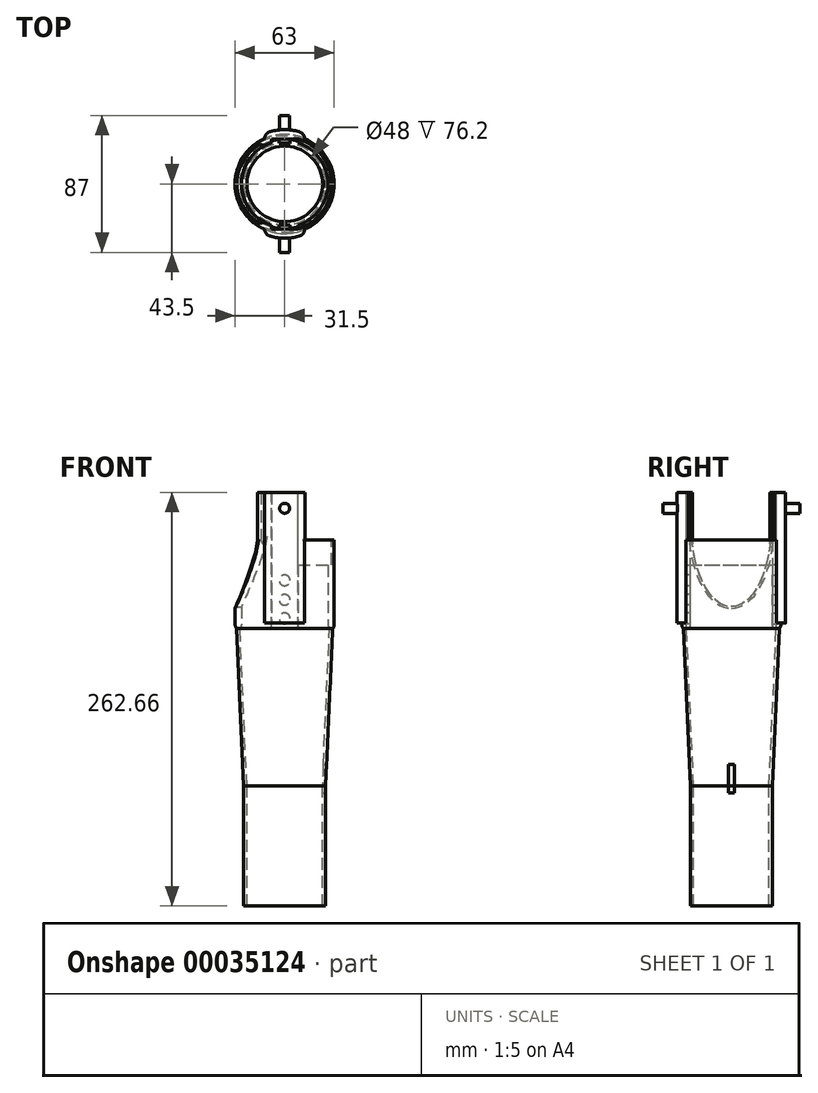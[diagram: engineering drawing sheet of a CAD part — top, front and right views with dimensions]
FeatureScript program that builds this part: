
annotation { "Feature Type Name" : "Feature", "Feature Type Description" : "" }
export const myFeature = defineFeature(function(context is Context, id is Id, definition is map)
    precondition{}
    {
        {
            var Q0;
            Q0=qCreatedBy(makeId("Top.planeOp"),FACE);
            var sketch = newSketch(context, id + "F0", { "sketchPlane" : qUnion([Q0])});
            skCircle(sketch, "E0", {"center": v(0, 0) * mm, "radius": 26 * mm});
            skSolve(sketch);
        }
        {
            var Q0;
            Q0=makeQuery(id+"F0.imprint","IMPRINT",FACE,{"disambiguationData":[TD([[makeQuery(id+"F0.imprint","IMPRINT",EDGE,{"derivedFrom":sQuery(id+"F0.wireOp",EDGE,"E0")}),1.0]])]});
            extrude(context, id + "F1", {"entities" : qUnion([Q0]), "depth" : 76.2 * mm});
        }
        {
            var Q0;
            Q0=makeQuery(id+"F1.opExtrude","CAP_FACE",FACE,{"disambiguationData":[OSD([sQuery(id+"F0.wireOp",EDGE,"E0")])],"isStart":false});
            cPlane(context, id + "F2", {"entities" : qUnion([Q0]), "cplaneType" : CPlaneType.OFFSET, "offset" : 0 * mm, "width" : 150 * mm, "height" : 150 * mm});
        }
        {
            var Q0;
            Q0=qCreatedBy(id+"F2.planeOp",FACE);
            var sketch = newSketch(context, id + "F3", { "sketchPlane" : qUnion([Q0])});
            skCircle(sketch, "E1.0", {"center": v(0, 0) * mm, "radius": 26 * mm});
            skSolve(sketch);
        }
        {
            var Q0;
            Q0=qCreatedBy(id+"F2.planeOp",FACE);
            cPlane(context, id + "F4", {"entities" : qUnion([Q0]), "cplaneType" : CPlaneType.OFFSET, "offset" : 100 * mm, "width" : 150 * mm, "height" : 150 * mm});
        }
        {
            var Q0;
            Q0=qCreatedBy(id+"F4.planeOp",FACE);
            var sketch = newSketch(context, id + "F5", { "sketchPlane" : qUnion([Q0])});
            skCircle(sketch, "E2", {"center": v(0, 0) * mm, "radius": 30.5 * mm});
            skSolve(sketch);
        }
        {
            var Q1;
            Q1=makeQuery(id+"F3.imprint","IMPRINT",FACE,{"disambiguationData":[TD([[makeQuery(id+"F3.imprint","IMPRINT",EDGE,{"derivedFrom":sQuery(id+"F3.wireOp",EDGE,"E1.0")}),1.0]])]});
            var Q2;
            Q2=makeQuery(id+"F5.imprint","IMPRINT",FACE,{"disambiguationData":[TD([[makeQuery(id+"F5.imprint","IMPRINT",EDGE,{"derivedFrom":sQuery(id+"F5.wireOp",EDGE,"E2")}),1.0]])]});
            loft(context, id + "F6", {"operationType" : NewBodyOperationType.ADD, "sheetProfilesArray" : [{ "sheetProfileEntities" : qUnion([Q1]) }, { "sheetProfileEntities" : qUnion([Q2]) }]});
        }
        {
            var Q0;
            Q0=qCreatedBy(id+"F2.planeOp",FACE);
            var sketch = newSketch(context, id + "F7", { "sketchPlane" : qUnion([Q0])});
            skCircle(sketch, "E3", {"center": v(0, 0) * mm, "radius": 24 * mm});
            skSolve(sketch);
        }
        {
            var Q0;
            Q0=qCreatedBy(id+"F4.planeOp",FACE);
            var sketch = newSketch(context, id + "F8", { "sketchPlane" : qUnion([Q0])});
            skCircle(sketch, "E4", {"center": v(0, 0) * mm, "radius": 28.5 * mm});
            skSolve(sketch);
        }
        {
            var Q1;
            Q1=makeQuery(id+"F8.imprint","IMPRINT",FACE,{"disambiguationData":[TD([[makeQuery(id+"F8.imprint","IMPRINT",EDGE,{"derivedFrom":sQuery(id+"F8.wireOp",EDGE,"E4")}),1.0]])]});
            var Q2;
            Q2 = qSketchRegion(id + "F7", true);
            loft(context, id + "F9", {"operationType" : NewBodyOperationType.REMOVE, "sheetProfilesArray" : [{ "sheetProfileEntities" : qUnion([Q1]) }, { "sheetProfileEntities" : qUnion([Q2]) }]});
        }
        {
            var Q0;
            Q0=qCreatedBy(makeId("Top.planeOp"),FACE);
            var sketch = newSketch(context, id + "F10", { "sketchPlane" : qUnion([Q0])});
            skCircle(sketch, "E5", {"center": v(0, 0) * mm, "radius": 24 * mm});
            skSolve(sketch);
        }
        {
            var Q1;
            Q1 = qSketchRegion(id + "F7", true);
            var Q2;
            Q2 = qSketchRegion(id + "F10", true);
            loft(context, id + "F11", {"operationType" : NewBodyOperationType.REMOVE, "sheetProfilesArray" : [{ "sheetProfileEntities" : qUnion([Q1]) }, { "sheetProfileEntities" : qUnion([Q2]) }]});
        }
        {
            var Q0;
            Q0=qCreatedBy(id+"F4.planeOp",FACE);
            var sketch = newSketch(context, id + "F12", { "sketchPlane" : qUnion([Q0])});
            skCircle(sketch, "E6", {"center": v(0, 0) * mm, "radius": 31.5 * mm});
            skCircle(sketch, "E7.0", {"center": v(0, 0) * mm, "radius": 27.5 * mm});
            skSolve(sketch);
        }
        {
            var Q0;
            Q0 = qSketchRegion(id + "F12", true);
            extrude(context, id + "F13", {"entities" : qUnion([Q0]), "operationType" : NewBodyOperationType.ADD, "depth" : 56.46 * mm});
        }
        {
            var Q0;
            Q0=makeQuery(id+"F13.opExtrude","CAP_EDGE",EDGE,{"disambiguationData":[OSD([sQuery(id+"F12.wireOp",EDGE,"E6")])],"isStart":true});
            fillet(context, id + "F14", {"entities" : qUnion([Q0]), "radius" : 5 * mm, "tangentPropagation" : true, "allowEdgeOverflow" : false});
        }
        {
            var Q0;
            Q0=makeQuery(id+"F13.opExtrude","CAP_FACE",FACE,{"disambiguationData":[OSD([sQuery(id+"F12.wireOp",EDGE,"E6"),sQuery(id+"F12.wireOp",EDGE,"E7.0")])],"isStart":false});
            cPlane(context, id + "F15", {"entities" : qUnion([Q0]), "cplaneType" : CPlaneType.OFFSET, "offset" : 0 * mm, "width" : 150 * mm, "height" : 150 * mm});
        }
        {
            var Q0;
            Q0=qCreatedBy(id+"F15.planeOp",FACE);
            var sketch = newSketch(context, id + "F16", { "sketchPlane" : qUnion([Q0])});
            skCircle(sketch, "E8.0", {"center": v(0, 0) * mm, "radius": 31.5 * mm, "construction": true});
            skCircle(sketch, "E9.0", {"center": v(0, 0) * mm, "radius": 27.5 * mm, "construction": true});
            skArc(sketch, "E10", {"start": v(8.5, -28.5) * mm, "mid": v(29.74, 0) * mm, "end": v(8.5, 28.5) * mm});
            skArc(sketch, "E11", {"start": v(8.5, -24.3) * mm, "mid": v(25.75, 0) * mm, "end": v(8.5, 24.3) * mm});
            skLineSegment(sketch, "E12", {"start": v(8.5, 28.5) * mm, "end": v(8.5, 24.3) * mm});
            skLineSegment(sketch, "E13.MirrorCS", {"start": v(8.5, -28.5) * mm, "end": v(8.5, -24.3) * mm});
            skPoint(sketch, "E14.orphan", {"position": v(0, 29.74) * mm});
            skPoint(sketch, "E15.orphan", {"position": v(0, -25.75) * mm});
            skSolve(sketch);
        }
        {
            var Q0;
            Q0 = qSketchRegion(id + "F16", true);
            extrude(context, id + "F17", {"entities" : qUnion([Q0]), "operationType" : NewBodyOperationType.REMOVE, "oppositeDirection" : true, "depth" : 16 * mm});
        }
        {
            var Q0;
            Q0=qCreatedBy(id+"F15.planeOp",FACE);
            var sketch = newSketch(context, id + "F18", { "sketchPlane" : qUnion([Q0])});
            skLineSegment(sketch, "E16.bottom", {"start": v(-8.5, 28.5) * mm, "end": v(8.5, 28.5) * mm});
            skLineSegment(sketch, "E16.top", {"start": v(-8.5, 24) * mm, "end": v(8.5, 24) * mm});
            skLineSegment(sketch, "E16.left", {"start": v(-8.5, 28.5) * mm, "end": v(-8.5, 24) * mm});
            skLineSegment(sketch, "E16.right", {"start": v(8.5, 28.5) * mm, "end": v(8.5, 24) * mm});
            skLineSegment(sketch, "E17", {"start": v(0, 28.5) * mm, "end": v(0, 24) * mm, "construction": true});
            skLineSegment(sketch, "E18.0", {"start": v(8.5, -28.5) * mm, "end": v(8.5, -28.5) * mm});
            skLineSegment(sketch, "E19.MirrorCS", {"start": v(-8.5, -24) * mm, "end": v(8.5, -24) * mm});
            skLineSegment(sketch, "E20.MirrorCS", {"start": v(8.5, -28.5) * mm, "end": v(8.5, -24) * mm});
            skLineSegment(sketch, "E21.MirrorCS", {"start": v(-8.5, -28.5) * mm, "end": v(8.5, -28.5) * mm});
            skLineSegment(sketch, "E22.MirrorCS", {"start": v(-8.5, -28.5) * mm, "end": v(-8.5, -24) * mm});
            skSolve(sketch);
        }
        {
            var Q0;
            Q0 = qSketchRegion(id + "F18", true);
            extrude(context, id + "F19", {"entities" : qUnion([Q0]), "operationType" : NewBodyOperationType.REMOVE, "oppositeDirection" : true, "depth" : 56.46 * mm});
        }
        {
            var Q0;
            {var subQ0=sQuery(id+"F12.wireOp",EDGE,"E7.0");Q0=makeQuery(id+"F19.boolean.opBoolean","SPLIT",EDGE,{"disambiguationData":[TD([makeQuery(id+"F19.opExtrude","SWEPT_FACE",FACE,{"disambiguationData":[OSD([sQuery(id+"F18.wireOp",EDGE,"E16.left")])]})])],"derivedFrom":makeQuery(id+"F13.opExtrude","CAP_EDGE",EDGE,{"disambiguationData":[OSD([subQ0])],"isStart":true})});}
            var Q1;
            {var subQ0=sQuery(id+"F12.wireOp",EDGE,"E7.0");Q1=makeQuery(id+"F19.boolean.opBoolean","SPLIT",EDGE,{"disambiguationData":[TD([makeQuery(id+"F19.opExtrude","SWEPT_FACE",FACE,{"disambiguationData":[OSD([sQuery(id+"F18.wireOp",EDGE,"E16.right")])]})])],"derivedFrom":makeQuery(id+"F13.opExtrude","CAP_EDGE",EDGE,{"disambiguationData":[OSD([subQ0])],"isStart":true})});}
            fillet(context, id + "F20", {"entities" : qUnion([Q0, Q1]), "radius" : 5 * mm, "tangentPropagation" : true, "allowEdgeOverflow" : false});
        }
        {
            var Q0;
            Q0=makeQuery(id+"F19.boolean.opBoolean","COPY",FACE,{"derivedFrom":makeQuery(id+"F19.opExtrude","SWEPT_FACE",FACE,{"disambiguationData":[OSD([sQuery(id+"F18.wireOp",EDGE,"E16.bottom")])]})});
            cPlane(context, id + "F21", {"entities" : qUnion([Q0]), "cplaneType" : CPlaneType.OFFSET, "offset" : 0 * mm, "width" : 150 * mm, "height" : 150 * mm});
        }
        {
            var Q0;
            Q0=qCreatedBy(id+"F21.planeOp",FACE);
            var sketch = newSketch(context, id + "F22", { "sketchPlane" : qUnion([Q0])});
            skLineSegment(sketch, "E23.0.0", {"start": v(8.5, 232.66) * mm, "end": v(-8.5, 232.66) * mm, "construction": true});
            skLineSegment(sketch, "E23.0.1", {"start": v(-8.5, 232.66) * mm, "end": v(-8.5, 176.2) * mm, "construction": true});
            skLineSegment(sketch, "E23.0.2", {"start": v(-8.5, 176.2) * mm, "end": v(0, 176.2) * mm, "construction": true});
            skLineSegment(sketch, "E23.0.3", {"start": v(0, 176.2) * mm, "end": v(8.5, 176.2) * mm, "construction": true});
            skLineSegment(sketch, "E23.0.4", {"start": v(8.5, 176.2) * mm, "end": v(8.5, 232.66) * mm, "construction": true});
            skLineSegment(sketch, "E24", {"start": v(0, 232.66) * mm, "end": v(0, 176.2) * mm, "construction": true});
            skCircle(sketch, "E25", {"center": v(0, 206.85) * mm, "radius": 3.45 * mm});
            skCircle(sketch, "E26", {"center": v(0, 194.54) * mm, "radius": 3.45 * mm});
            skCircle(sketch, "E27", {"center": v(0, 182.7) * mm, "radius": 3.45 * mm});
            skSolve(sketch);
        }
        {
            var Q0;
            Q0 = qSketchRegion(id + "F22", true);
            extrude(context, id + "F23", {"entities" : qUnion([Q0]), "depth" : 2.5 * mm});
        }
        {
            var Q0;
            Q0=makeQuery(id+"F23.opExtrude","SWEPT_BODY",BODY,{"disambiguationData":[OSD([sQuery(id+"F22.wireOp",EDGE,"E25")])]});
            var Q1;
            Q1=makeQuery(id+"F23.opExtrude","SWEPT_BODY",BODY,{"disambiguationData":[OSD([sQuery(id+"F22.wireOp",EDGE,"E26")])]});
            var Q2;
            Q2=makeQuery(id+"F23.opExtrude","SWEPT_BODY",BODY,{"disambiguationData":[OSD([sQuery(id+"F22.wireOp",EDGE,"E27")])]});
            var Q3;
            Q3=qCreatedBy(makeId("Front.planeOp"),FACE);
            mirror(context, id + "F24", {"operationType" : NewBodyOperationType.ADD, "entities" : qUnion([Q0, Q1, Q2]), "mirrorPlane" : qUnion([Q3])});
        }
        {
            var Q0;
            Q0=qCreatedBy(id+"F15.planeOp",FACE);
            var sketch = newSketch(context, id + "F25", { "sketchPlane" : qUnion([Q0])});
            skCircle(sketch, "E28", {"center": v(0, 0) * mm, "radius": 34.44 * mm});
            skCircle(sketch, "E29.0", {"center": v(0, 0) * mm, "radius": 31.5 * mm});
            skLineSegment(sketch, "E30", {"start": v(12.77, 31.98) * mm, "end": v(12.77, 28.8) * mm});
            skLineSegment(sketch, "E31.MirrorCS", {"start": v(-12.77, 31.98) * mm, "end": v(-12.77, 28.8) * mm});
            skLineSegment(sketch, "E32.MirrorCS", {"start": v(12.77, -31.98) * mm, "end": v(12.77, -28.8) * mm});
            skLineSegment(sketch, "E33.MirrorCS", {"start": v(-12.77, -31.98) * mm, "end": v(-12.77, -28.8) * mm});
            skSolve(sketch);
        }
        {
            var Q0;
            {var subQ1=sQuery(id+"F25.wireOp",EDGE,"E30");Q0=makeQuery(id+"F25.imprint","IMPRINT",FACE,{"disambiguationData":[TD([[makeQuery(id+"F25.imprint","IMPRINT",EDGE,{"derivedFrom":subQ1}),-1.0]])]});}
            var Q1;
            {var subQ1=sQuery(id+"F25.wireOp",EDGE,"E32.MirrorCS");Q1=makeQuery(id+"F25.imprint","IMPRINT",FACE,{"disambiguationData":[TD([[makeQuery(id+"F25.imprint","IMPRINT",EDGE,{"derivedFrom":subQ1}),1.0]])]});}
            extrude(context, id + "F26", {"entities" : qUnion([Q0, Q1]), "operationType" : NewBodyOperationType.ADD, "depth" : 30 * mm, "hasSecondDirection" : true, "secondDirectionOppositeDirection" : true, "secondDirectionDepth" : 53 * mm});
        }
        {
            var Q0;
            Q0=makeQuery(id+"F13.opExtrude","CAP_FACE",FACE,{"disambiguationData":[OSD([sQuery(id+"F12.wireOp",EDGE,"E6"),sQuery(id+"F12.wireOp",EDGE,"E7.0")])],"isStart":false});
            var sketch = newSketch(context, id + "F27", { "sketchPlane" : qUnion([Q0])});
            skLineSegment(sketch, "E34", {"start": v(12.77, 28.8) * mm, "end": v(12.77, 26.86) * mm});
            skLineSegment(sketch, "E35", {"start": v(-12.77, 28.8) * mm, "end": v(-12.77, 24.35) * mm});
            skLineSegment(sketch, "E36.MirrorCS", {"start": v(12.77, -28.8) * mm, "end": v(12.77, -26.86) * mm});
            skLineSegment(sketch, "E37.MirrorCS", {"start": v(-12.77, -28.8) * mm, "end": v(-12.77, -24.35) * mm});
            skSolve(sketch);
        }
        {
            var Q0;
            {var subQ5=sQuery(id+"F27.wireOp",EDGE,"E34");Q0=makeQuery(id+"F27.imprint","IMPRINT",FACE,{"disambiguationData":[TD([[makeQuery(id+"F27.imprint","IMPRINT",EDGE,{"derivedFrom":subQ5}),-1.0]])]});}
            var Q1;
            {var subQ9=sQuery(id+"F27.wireOp",EDGE,"E36.MirrorCS");Q1=makeQuery(id+"F27.imprint","IMPRINT",FACE,{"disambiguationData":[TD([[makeQuery(id+"F27.imprint","IMPRINT",EDGE,{"derivedFrom":subQ9}),1.0]])]});}
            extrude(context, id + "F28", {"entities" : qUnion([Q0, Q1]), "operationType" : NewBodyOperationType.ADD, "depth" : 30 * mm, "hasSecondDirection" : true, "secondDirectionOppositeDirection" : true, "secondDirectionDepth" : 25 * mm});
        }
        {
            var Q0;
            Q0=makeQuery(id+"F26.opExtrude","SWEPT_EDGE",EDGE,{"disambiguationData":[OSD([sQuery(id+"F25.wireOp",EDGE,"E28"),sQuery(id+"F25.wireOp",EDGE,"E31.MirrorCS")])]});
            var Q1;
            Q1=makeQuery(id+"F26.opExtrude","SWEPT_EDGE",EDGE,{"disambiguationData":[OSD([sQuery(id+"F25.wireOp",EDGE,"E28"),sQuery(id+"F25.wireOp",EDGE,"E33.MirrorCS")])]});
            var Q2;
            Q2=makeQuery(id+"F26.opExtrude","SWEPT_EDGE",EDGE,{"disambiguationData":[OSD([sQuery(id+"F25.wireOp",EDGE,"E28"),sQuery(id+"F25.wireOp",EDGE,"E32.MirrorCS")])]});
            var Q3;
            Q3=makeQuery(id+"F26.opExtrude","SWEPT_EDGE",EDGE,{"disambiguationData":[OSD([sQuery(id+"F25.wireOp",EDGE,"E28"),sQuery(id+"F25.wireOp",EDGE,"E30")])]});
            fillet(context, id + "F29", {"entities" : qUnion([Q0, Q1, Q2, Q3]), "radius" : 5 * mm, "tangentPropagation" : true, "allowEdgeOverflow" : false});
        }
        {
            var Q0;
            Q0=makeQuery(id+"F28.opExtrude","SWEPT_EDGE",EDGE,{"disambiguationData":[OSD([sQuery(id+"F12.wireOp",EDGE,"E7.0"),sQuery(id+"F27.wireOp",EDGE,"E37.MirrorCS")])]});
            fillet(context, id + "F30", {"entities" : qUnion([Q0]), "radius" : 1 * mm, "tangentPropagation" : true, "allowEdgeOverflow" : false});
        }
        {
            var Q0;
            Q0=makeQuery(id+"F28.opExtrude","SWEPT_EDGE",EDGE,{"disambiguationData":[OSD([sQuery(id+"F12.wireOp",EDGE,"E7.0"),sQuery(id+"F27.wireOp",EDGE,"E35")])]});
            fillet(context, id + "F31", {"entities" : qUnion([Q0]), "radius" : 1 * mm, "tangentPropagation" : true, "allowEdgeOverflow" : false});
        }
        {
            var Q0;
            Q0=makeQuery(id+"F28.opExtrude","SWEPT_EDGE",EDGE,{"disambiguationData":[OSD([sQuery(id+"F16.wireOp",EDGE,"E10"),sQuery(id+"F27.wireOp",EDGE,"E36.MirrorCS")])]});
            fillet(context, id + "F32", {"entities" : qUnion([Q0]), "radius" : 1 * mm, "tangentPropagation" : true, "allowEdgeOverflow" : false});
        }
        {
            var Q0;
            Q0=makeQuery(id+"F28.opExtrude","SWEPT_EDGE",EDGE,{"disambiguationData":[OSD([sQuery(id+"F16.wireOp",EDGE,"E10"),sQuery(id+"F27.wireOp",EDGE,"E34")])]});
            fillet(context, id + "F33", {"entities" : qUnion([Q0]), "radius" : 1 * mm, "tangentPropagation" : true, "allowEdgeOverflow" : false});
        }
        {
            var Q0;
            {var subQ0=sQuery(id+"F18.wireOp",EDGE,"E16.bottom");Q0=makeQuery(id+"F28.boolean.opBoolean","MERGE",FACE,{"derivedFrom":[makeQuery(id+"F19.boolean.opBoolean","COPY",FACE,{"derivedFrom":makeQuery(id+"F19.opExtrude","SWEPT_FACE",FACE,{"disambiguationData":[OSD([subQ0])]})}),makeQuery(id+"F28.opExtrude","SWEPT_FACE",FACE,{"disambiguationData":[OSD([subQ0])]})]});}
            var sketch = newSketch(context, id + "F34", { "sketchPlane" : qUnion([Q0])});
            skLineSegment(sketch, "E38.0", {"start": v(-8.5, 262.66) * mm, "end": v(8.5, 262.66) * mm, "construction": true});
            skLineSegment(sketch, "E39", {"start": v(0, 262.66) * mm, "end": v(0, 242.66) * mm, "construction": true});
            skPoint(sketch, "E39.endSnap0", {"position": v(0, 262.66) * mm});
            skCircle(sketch, "E40", {"center": v(0, 252.66) * mm, "radius": 3.18 * mm});
            skSolve(sketch);
        }
        {
            var Q0;
            Q0=makeQuery(id+"F34.imprint","IMPRINT",FACE,{"disambiguationData":[TD([[makeQuery(id+"F34.imprint","IMPRINT",EDGE,{"derivedFrom":sQuery(id+"F34.wireOp",EDGE,"E40")}),1.0]])]});
            extrude(context, id + "F35", {"entities" : qUnion([Q0]), "oppositeDirection" : true, "depth" : 15 * mm});
        }
        {
            var Q0;
            Q0=makeQuery(id+"F35.opExtrude","SWEPT_BODY",BODY,{"disambiguationData":[OSD([sQuery(id+"F34.wireOp",EDGE,"E40")])]});
            var Q1;
            Q1=qCreatedBy(makeId("Front.planeOp"),FACE);
            mirror(context, id + "F36", {"operationType" : NewBodyOperationType.ADD, "entities" : qUnion([Q0]), "mirrorPlane" : qUnion([Q1])});
        }
        {
            var Q0;
            Q0=qCreatedBy(makeId("Right.planeOp"),FACE);
            cPlane(context, id + "F37", {"entities" : qUnion([Q0]), "cplaneType" : CPlaneType.OFFSET, "offset" : 55 * mm, "oppositeDirection" : true, "width" : 150 * mm, "height" : 150 * mm});
        }
        {
            var Q0;
            Q0=qCreatedBy(id+"F37.planeOp",FACE);
            var sketch = newSketch(context, id + "F38", { "sketchPlane" : qUnion([Q0])});
            skLineSegment(sketch, "E41", {"start": v(-31.5, 188.04) * mm, "end": v(-31.5, 188.5) * mm, "construction": true});
            skLineSegment(sketch, "E42", {"start": v(31.5, 188.5) * mm, "end": v(31.5, 188.04) * mm, "construction": true});
            skEllipse(sketch, "E43", {"center": v(0, 241.57) * mm, "majorRadius": 25.3 * mm, "minorRadius": 51.5 * mm, "majorAxis": v(-1, 0)});
            skSolve(sketch);
        }
        {
            var Q0;
            Q0 = qSketchRegion(id + "F38", true);
            extrude(context, id + "F39", {"entities" : qUnion([Q0]), "operationType" : NewBodyOperationType.REMOVE, "depth" : 40 * mm});
        }
        {
            var Q0;
            Q0=makeQuery(id+"F39.boolean.opBoolean","INTERSECT",EDGE,{"derivedFrom":[makeQuery(id+"F13.opExtrude","SWEPT_FACE",FACE,{"disambiguationData":[OSD([sQuery(id+"F12.wireOp",EDGE,"E6")])]}),makeQuery(id+"F39.opExtrude","SWEPT_FACE",FACE,{"disambiguationData":[OSD([sQuery(id+"F38.wireOp",EDGE,"E43")])]})]});
            fillet(context, id + "F40", {"entities" : qUnion([Q0]), "radius" : 1 * mm, "tangentPropagation" : true, "allowEdgeOverflow" : false});
        }
        {
            var Q0;
            {var subQ0=sQuery(id+"F12.wireOp",EDGE,"E6");var subQ1=sQuery(id+"F12.wireOp",EDGE,"E7.0");var subQ6=sQuery(id+"F25.wireOp",EDGE,"E33.MirrorCS");var subQ7=makeQuery(id+"F26.opExtrude","SWEPT_FACE",FACE,{"disambiguationData":[OSD([subQ6])]});Q0=makeQuery(id+"F39.boolean.opBoolean","SPLIT",FACE,{"disambiguationData":[TD([subQ7])],"derivedFrom":makeQuery(id+"F28.boolean.opBoolean","SPLIT",FACE,{"disambiguationData":[TD([makeQuery(id+"F13.opExtrude","SWEPT_FACE",FACE,{"disambiguationData":[OSD([subQ1])]})])],"derivedFrom":makeQuery(id+"F13.opExtrude","CAP_FACE",FACE,{"disambiguationData":[OSD([subQ0,subQ1])],"isStart":false})})});}
            var Q1;
            {var subQ0=sQuery(id+"F12.wireOp",EDGE,"E6");var subQ1=sQuery(id+"F12.wireOp",EDGE,"E7.0");var subQ6=sQuery(id+"F25.wireOp",EDGE,"E31.MirrorCS");var subQ7=makeQuery(id+"F26.opExtrude","SWEPT_FACE",FACE,{"disambiguationData":[OSD([subQ6])]});Q1=makeQuery(id+"F39.boolean.opBoolean","SPLIT",FACE,{"disambiguationData":[TD([subQ7])],"derivedFrom":makeQuery(id+"F28.boolean.opBoolean","SPLIT",FACE,{"disambiguationData":[TD([makeQuery(id+"F13.opExtrude","SWEPT_FACE",FACE,{"disambiguationData":[OSD([subQ1])]})])],"derivedFrom":makeQuery(id+"F13.opExtrude","CAP_FACE",FACE,{"disambiguationData":[OSD([subQ0,subQ1])],"isStart":false})})});}
            var Q2;
            Q2=makeQuery(id+"F28.boolean.opBoolean","MERGE",FACE,{"derivedFrom":[makeQuery(id+"F26.opExtrude","CAP_FACE",FACE,{"disambiguationData":[OSD([sQuery(id+"F25.wireOp",EDGE,"E28"),sQuery(id+"F25.wireOp",EDGE,"E29.0"),sQuery(id+"F25.wireOp",EDGE,"E32.MirrorCS"),sQuery(id+"F25.wireOp",EDGE,"E33.MirrorCS")])],"isStart":false}),makeQuery(id+"F28.opExtrude","CAP_FACE",FACE,{"disambiguationData":[OSD([sQuery(id+"F12.wireOp",EDGE,"E6"),sQuery(id+"F12.wireOp",EDGE,"E7.0"),sQuery(id+"F16.wireOp",EDGE,"E10"),sQuery(id+"F18.wireOp",EDGE,"E20.MirrorCS"),sQuery(id+"F18.wireOp",EDGE,"E21.MirrorCS"),sQuery(id+"F18.wireOp",EDGE,"E22.MirrorCS"),sQuery(id+"F27.wireOp",EDGE,"E36.MirrorCS"),sQuery(id+"F27.wireOp",EDGE,"E37.MirrorCS")])],"isStart":false})]});
            extrude(context, id + "F41", {"entities" : qUnion([Q0, Q1]), "operationType" : NewBodyOperationType.ADD, "endBound" : BoundingType.UP_TO_SURFACE, "endBoundEntityFace" : qUnion([Q2]), "depth" : 25 * mm});
        }
        {
            var Q0;
            {var subQ0=sQuery(id+"F38.wireOp",EDGE,"E43");var subQ1=makeQuery(id+"F39.opExtrude","CAP_FACE",FACE,{"disambiguationData":[OSD([subQ0])],"isStart":false});var subQ2=sQuery(id+"F12.wireOp",EDGE,"E7.0");var subQ3=makeQuery(id+"F13.opExtrude","SWEPT_FACE",FACE,{"disambiguationData":[OSD([subQ2])]});var subQ5=sQuery(id+"F12.wireOp",EDGE,"E6");var subQ7=makeQuery(id+"F13.opExtrude","CAP_EDGE",EDGE,{"disambiguationData":[OSD([subQ2])],"isStart":false});var subQ8=sQuery(id+"F18.wireOp",EDGE,"E16.left");var subQ9=makeQuery(id+"F28.opExtrude","SWEPT_FACE",FACE,{"disambiguationData":[OSD([subQ2]),TDD([makeQuery(id+"F27.imprint","IMPRINT",EDGE,{"disambiguationData":[TD([[makeQuery(id+"F27.imprint","INTERSECT",VERTEX,{"derivedFrom":[makeQuery(id+"F19.boolean.opBoolean","COPY",EDGE,{"derivedFrom":makeQuery(id+"F19.opExtrude","CAP_EDGE",EDGE,{"disambiguationData":[OSD([subQ8])],"isStart":true})}),subQ7]}),1.0]])],"derivedFrom":subQ7})])]});var subQ10=sQuery(id+"F18.wireOp",EDGE,"E22.MirrorCS");var subQ11=makeQuery(id+"F28.opExtrude","SWEPT_FACE",FACE,{"disambiguationData":[OSD([subQ2]),TDD([makeQuery(id+"F27.imprint","IMPRINT",EDGE,{"disambiguationData":[TD([[makeQuery(id+"F27.imprint","INTERSECT",VERTEX,{"derivedFrom":[makeQuery(id+"F19.boolean.opBoolean","COPY",EDGE,{"derivedFrom":makeQuery(id+"F19.opExtrude","CAP_EDGE",EDGE,{"disambiguationData":[OSD([subQ10])],"isStart":true})}),subQ7]}),-1.0]])],"derivedFrom":subQ7})])]});var subQ12=makeQuery(id+"F13.opExtrude","CAP_FACE",FACE,{"disambiguationData":[OSD([subQ5,subQ2])],"isStart":false});var subQ13=makeQuery(id+"F28.boolean.opBoolean","MERGE",FACE,{"derivedFrom":[makeQuery(id+"F19.boolean.opBoolean","SPLIT",FACE,{"disambiguationData":[TD([makeQuery(id+"F19.opExtrude","SWEPT_FACE",FACE,{"disambiguationData":[OSD([subQ8])]})])],"derivedFrom":subQ3}),subQ9,subQ11]});Q0=makeQuery(id+"F41.boolean.opBoolean","MERGE",EDGE,{"derivedFrom":[makeQuery(id+"F39.boolean.opBoolean","INTERSECT",EDGE,{"disambiguationData":[OD(0.0)],"derivedFrom":[subQ13,subQ1]}),makeQuery(id+"F41.opExtrude","SWEPT_EDGE",EDGE,{"disambiguationData":[OSD([subQ5,subQ2,subQ0]),TDD([makeQuery(id+"F39.boolean.opBoolean","INTERSECT",VERTEX,{"disambiguationData":[OD(0.0)],"derivedFrom":[subQ13,makeQuery(id+"F28.boolean.opBoolean","SPLIT",FACE,{"disambiguationData":[TD([subQ3])],"derivedFrom":subQ12}),subQ1]})])]})]});}
            var Q1;
            {var subQ0=sQuery(id+"F38.wireOp",EDGE,"E43");var subQ1=makeQuery(id+"F39.opExtrude","CAP_FACE",FACE,{"disambiguationData":[OSD([subQ0])],"isStart":false});var subQ2=sQuery(id+"F12.wireOp",EDGE,"E7.0");var subQ3=makeQuery(id+"F13.opExtrude","SWEPT_FACE",FACE,{"disambiguationData":[OSD([subQ2])]});var subQ5=sQuery(id+"F12.wireOp",EDGE,"E6");var subQ7=makeQuery(id+"F13.opExtrude","CAP_EDGE",EDGE,{"disambiguationData":[OSD([subQ2])],"isStart":false});var subQ8=sQuery(id+"F18.wireOp",EDGE,"E16.left");var subQ9=makeQuery(id+"F28.opExtrude","SWEPT_FACE",FACE,{"disambiguationData":[OSD([subQ2]),TDD([makeQuery(id+"F27.imprint","IMPRINT",EDGE,{"disambiguationData":[TD([[makeQuery(id+"F27.imprint","INTERSECT",VERTEX,{"derivedFrom":[makeQuery(id+"F19.boolean.opBoolean","COPY",EDGE,{"derivedFrom":makeQuery(id+"F19.opExtrude","CAP_EDGE",EDGE,{"disambiguationData":[OSD([subQ8])],"isStart":true})}),subQ7]}),1.0]])],"derivedFrom":subQ7})])]});var subQ10=sQuery(id+"F18.wireOp",EDGE,"E22.MirrorCS");var subQ11=makeQuery(id+"F28.opExtrude","SWEPT_FACE",FACE,{"disambiguationData":[OSD([subQ2]),TDD([makeQuery(id+"F27.imprint","IMPRINT",EDGE,{"disambiguationData":[TD([[makeQuery(id+"F27.imprint","INTERSECT",VERTEX,{"derivedFrom":[makeQuery(id+"F19.boolean.opBoolean","COPY",EDGE,{"derivedFrom":makeQuery(id+"F19.opExtrude","CAP_EDGE",EDGE,{"disambiguationData":[OSD([subQ10])],"isStart":true})}),subQ7]}),-1.0]])],"derivedFrom":subQ7})])]});var subQ12=makeQuery(id+"F13.opExtrude","CAP_FACE",FACE,{"disambiguationData":[OSD([subQ5,subQ2])],"isStart":false});var subQ13=makeQuery(id+"F28.boolean.opBoolean","MERGE",FACE,{"derivedFrom":[makeQuery(id+"F19.boolean.opBoolean","SPLIT",FACE,{"disambiguationData":[TD([makeQuery(id+"F19.opExtrude","SWEPT_FACE",FACE,{"disambiguationData":[OSD([subQ8])]})])],"derivedFrom":subQ3}),subQ9,subQ11]});Q1=makeQuery(id+"F41.boolean.opBoolean","MERGE",EDGE,{"derivedFrom":[makeQuery(id+"F39.boolean.opBoolean","INTERSECT",EDGE,{"disambiguationData":[OD(1.0)],"derivedFrom":[subQ13,subQ1]}),makeQuery(id+"F41.opExtrude","SWEPT_EDGE",EDGE,{"disambiguationData":[OSD([subQ5,subQ2,subQ0]),TDD([makeQuery(id+"F39.boolean.opBoolean","INTERSECT",VERTEX,{"disambiguationData":[OD(1.0)],"derivedFrom":[subQ13,makeQuery(id+"F28.boolean.opBoolean","SPLIT",FACE,{"disambiguationData":[TD([subQ3])],"derivedFrom":subQ12}),subQ1]})])]})]});}
            fillet(context, id + "F42", {"entities" : qUnion([Q0, Q1]), "radius" : 5 * mm, "tangentPropagation" : true, "allowEdgeOverflow" : false});
        }
        {
            var Q0;
            Q0=qCreatedBy(makeId("Right.planeOp"),FACE);
            cPlane(context, id + "F43", {"entities" : qUnion([Q0]), "cplaneType" : CPlaneType.OFFSET, "offset" : 30 * mm, "width" : 150 * mm, "height" : 150 * mm});
        }
        {
            var Q0;
            Q0=qCreatedBy(id+"F43.planeOp",FACE);
            var sketch = newSketch(context, id + "F44", { "sketchPlane" : qUnion([Q0])});
            skLineSegment(sketch, "E44", {"start": v(-32.6, 89.9) * mm, "end": v(32.63, 89.9) * mm, "construction": true});
            skLineSegment(sketch, "E45.bottom", {"start": v(2.02, 89.9) * mm, "end": v(-1.98, 89.9) * mm});
            skLineSegment(sketch, "E45.top", {"start": v(2.02, 71.9) * mm, "end": v(-1.98, 71.9) * mm});
            skLineSegment(sketch, "E45.left", {"start": v(2.02, 89.9) * mm, "end": v(2.02, 71.9) * mm});
            skLineSegment(sketch, "E45.right", {"start": v(-1.98, 89.9) * mm, "end": v(-1.98, 71.9) * mm});
            skPoint(sketch, "E45.middle", {"position": v(0.02, 80.9) * mm});
            skPoint(sketch, "E45.middle.positionSnap0", {"position": v(0.02, 89.9) * mm});
            skPoint(sketch, "E45.centerSnap0", {"position": v(0.02, 89.9) * mm});
            skSolve(sketch);
        }
        {
            var Q0;
            Q0 = qSketchRegion(id + "F44", true);
            extrude(context, id + "F45", {"entities" : qUnion([Q0]), "operationType" : NewBodyOperationType.REMOVE, "oppositeDirection" : true, "depth" : 25 * mm});
        }
    });
